# Revit family: Petal_CB-295M_BIM
name_source: partatom
category: Arredi
units: mm (PartAtom-declared; Revit-internal decimal feet)

## family parameters
Attiva taglio nelle viste = No
Basato su piano di lavoro = No
Condiviso = No
Numero OmniClass = 23.40.20.00
Origine composizione di rendering = Geometria famiglia
Punto di calcolo locali = No
Sempre verticale = Sì
Taglio con vuoti quando caricato = No
Titolo OmniClass = General Furniture and Specialties

## types (2) — shared parameters
AVAILABLE FINISHES = Ebonized black lacquer on Oak (EB). Raw effect lacquer on Oak (RE). Natural lacquer on Oak or Walnut (NC). Base: smoke powder coat finish (SP).
BASE MATERIAL = BASSAM_FELLOWS_OAK_O-NA
BIM BADGE = https://bim.archiproducts.com
COLLECTION = Petal
DEPTH = 648 mm
Descrizione = Wood and steel lounge chair with armrests
HEIGHT = 675 mm
PILLOW MATERIAL = BASSAM_FELLOWS_ELEGANT_LEATHER_48027_OLIVE
PRODUCT SHEET = https://www.archiproducts.com
Produttore = BassamFellows
STRUCTURE MATERIAL = <Per categoria>
TECHNICAL SHEET = https://bassamfellows.com
UPHOLSTERY MATERIAL = BASSAM_FELLOWS_COMFORT_LEATHER_43632_CAMEL
URL = https://bassamfellows.com
WIDTH = 689 mm
zero-valued in all types: Prospetto di default

## per-type parameters (varying)
| type | MATERIAL DESCRIPTION | Modello | PRODUCT CODE |
| CB-295M_Cushion | Tubular steel base. 3D veneer plywood shell. Dense foam seat pad with welt detail. | Petal Lounge Armchair Metal Base with Cushion | CB-295M_CB-134 |
| CB-295M | Tubular steel base. 3D veneer plywood shell. | Petal Lounge Armchair Metal Base | CB-295M |

## geometry (parser evidence)
native form markers: Sweep x1
no freeform markers — native parametric forms only
